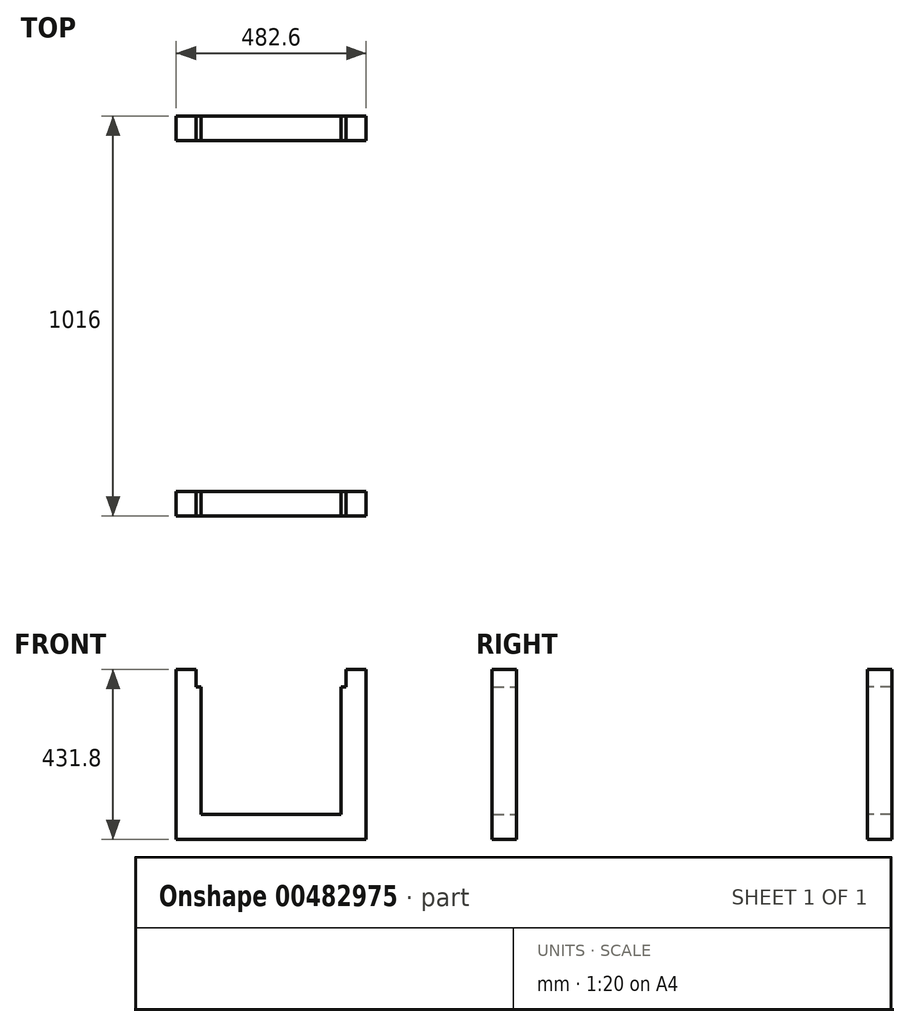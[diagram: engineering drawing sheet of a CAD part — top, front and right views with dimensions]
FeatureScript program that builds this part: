
annotation { "Feature Type Name" : "Feature", "Feature Type Description" : "" }
export const myFeature = defineFeature(function(context is Context, id is Id, definition is map)
    precondition{}
    {
        {
            var Q0;
            Q0=qCreatedBy(makeId("Front.planeOp"),FACE);
            var sketch = newSketch(context, id + "F0", { "sketchPlane" : qUnion([Q0])});
            skLineSegment(sketch, "E0.bottom", {"start": v(-93.2, 0) * mm, "end": v(-29.7, 0) * mm});
            skLineSegment(sketch, "E0.top", {"start": v(-93.2, -431.8) * mm, "end": v(-29.7, -431.8) * mm});
            skLineSegment(sketch, "E0.left", {"start": v(-93.2, 0) * mm, "end": v(-93.2, -431.8) * mm});
            skLineSegment(sketch, "E0.right", {"start": v(-29.7, 0) * mm, "end": v(-29.7, -431.8) * mm});
            skLineSegment(sketch, "E1.bottom", {"start": v(-93.2, 0) * mm, "end": v(389.4, 0) * mm});
            skLineSegment(sketch, "E1.top", {"start": v(-93.2, -431.8) * mm, "end": v(389.4, -431.8) * mm});
            skLineSegment(sketch, "E1.right", {"start": v(389.4, 0) * mm, "end": v(389.4, -431.8) * mm});
            skLineSegment(sketch, "E2.bottom", {"start": v(389.4, 0) * mm, "end": v(325.9, 0) * mm});
            skLineSegment(sketch, "E2.top", {"start": v(389.4, -431.8) * mm, "end": v(325.9, -431.8) * mm});
            skLineSegment(sketch, "E2.right", {"start": v(325.9, 0) * mm, "end": v(325.9, -431.8) * mm});
            skLineSegment(sketch, "E3.bottom", {"start": v(-29.7, -431.8) * mm, "end": v(325.9, -431.8) * mm});
            skLineSegment(sketch, "E3.top", {"start": v(-29.7, -368.3) * mm, "end": v(325.9, -368.3) * mm});
            skLineSegment(sketch, "E3.left", {"start": v(-29.7, -431.8) * mm, "end": v(-29.7, -368.3) * mm});
            skLineSegment(sketch, "E3.right", {"start": v(325.9, -431.8) * mm, "end": v(325.9, -368.3) * mm});
            skLineSegment(sketch, "E4.bottom", {"start": v(-29.7, 0) * mm, "end": v(-42.4, 0) * mm});
            skLineSegment(sketch, "E4.top", {"start": v(-29.7, -44.45) * mm, "end": v(-42.4, -44.45) * mm});
            skLineSegment(sketch, "E4.left", {"start": v(-29.7, 0) * mm, "end": v(-29.7, -44.45) * mm});
            skLineSegment(sketch, "E4.right", {"start": v(-42.4, 0) * mm, "end": v(-42.4, -44.45) * mm});
            skLineSegment(sketch, "E5", {"start": v(148.1, -431.8) * mm, "end": v(148.1, 0) * mm});
            skLineSegment(sketch, "E6.MirrorCS", {"start": v(325.9, -44.45) * mm, "end": v(338.6, -44.45) * mm});
            skLineSegment(sketch, "E7.MirrorCS", {"start": v(338.6, 0) * mm, "end": v(338.6, -44.45) * mm});
            skLineSegment(sketch, "E8.MirrorCS", {"start": v(325.9, 0) * mm, "end": v(338.6, 0) * mm});
            skLineSegment(sketch, "E9.MirrorCS", {"start": v(325.9, 0) * mm, "end": v(325.9, -44.45) * mm});
            skSolve(sketch);
        }
        {
            var Q0;
            {var subQ4=sQuery(id+"F0.wireOp",EDGE,"E0.top");Q0=makeQuery(id+"F0.imprint","IMPRINT",FACE,{"disambiguationData":[TD([[makeQuery(id+"F0.imprint","IMPRINT",EDGE,{"derivedFrom":subQ4}),1.0]])]});}
            var Q1;
            {var subQ1=sQuery(id+"F0.wireOp",EDGE,"E0.right");var subQ3=sQuery(id+"F0.wireOp",EDGE,"E3.top");var subQ4=makeQuery(id+"F0.imprint","INTERSECT",VERTEX,{"derivedFrom":[subQ1,subQ3]});Q1=makeQuery(id+"F0.imprint","IMPRINT",FACE,{"disambiguationData":[TD([[makeQuery(id+"F0.imprint","IMPRINT",EDGE,{"disambiguationData":[TD([[subQ4,-1.0]])],"derivedFrom":subQ3}),-1.0]])]});}
            var Q2;
            {var subQ0=sQuery(id+"F0.wireOp",EDGE,"E5");var subQ1=sQuery(id+"F0.wireOp",EDGE,"E1.top");var subQ2=makeQuery(id+"F0.imprint","INTERSECT",VERTEX,{"derivedFrom":[subQ1,subQ0]});Q2=makeQuery(id+"F0.imprint","IMPRINT",FACE,{"disambiguationData":[TD([[makeQuery(id+"F0.imprint","IMPRINT",EDGE,{"disambiguationData":[TD([[subQ2,-1.0]])],"derivedFrom":subQ1}),1.0]])]});}
            var Q3;
            {var subQ3=sQuery(id+"F0.wireOp",EDGE,"E1.right");Q3=makeQuery(id+"F0.imprint","IMPRINT",FACE,{"disambiguationData":[TD([[makeQuery(id+"F0.imprint","IMPRINT",EDGE,{"derivedFrom":subQ3}),-1.0]])]});}
            extrude(context, id + "F1", {"entities" : qUnion([Q0, Q1, Q2, Q3]), "depth" : 61.9 * mm, "offsetDistance" : 25.4 * mm});
        }
        {
            var Q0;
            Q0=sQuery(id+"F0.wireOp",EDGE,"E5");
            cPlane(context, id + "F2", {"entities" : qUnion([Q0]), "cplaneType" : CPlaneType.LINE_ANGLE, "offset" : 25.4 * mm, "angle" : 0 * degree, "width" : 152.4 * mm, "height" : 152.4 * mm});
        }
        {
            var Q0;
            Q0=qCreatedBy(id+"F2.planeOp",FACE);
            var sketch = newSketch(context, id + "F3", { "sketchPlane" : qUnion([Q0])});
            skLineSegment(sketch, "E10.bottom", {"start": v(-61.91, 0) * mm, "end": v(954.09, 0) * mm});
            skLineSegment(sketch, "E10.top", {"start": v(-61.91, -431.8) * mm, "end": v(954.09, -431.8) * mm});
            skLineSegment(sketch, "E10.left", {"start": v(-61.91, 0) * mm, "end": v(-61.91, -431.8) * mm});
            skLineSegment(sketch, "E10.right", {"start": v(954.09, 0) * mm, "end": v(954.09, -431.8) * mm});
            skLineSegment(sketch, "E11", {"start": v(446.09, 0) * mm, "end": v(446.09, -431.8) * mm});
            skSolve(sketch);
        }
        {
            var Q0;
            Q0=sQuery(id+"F3.wireOp",EDGE,"E11");
            cPlane(context, id + "F4", {"entities" : qUnion([Q0]), "cplaneType" : CPlaneType.LINE_ANGLE, "offset" : 25.4 * mm, "angle" : 90 * degree, "width" : 152.4 * mm, "height" : 152.4 * mm});
        }
        {
            var Q0;
            Q0=makeQuery(id+"F1.opExtrude","SWEPT_BODY",BODY,{"disambiguationData":[OSD([sQuery(id+"F0.wireOp",EDGE,"E0.bottom"),sQuery(id+"F0.wireOp",EDGE,"E0.top"),sQuery(id+"F0.wireOp",EDGE,"E0.left"),sQuery(id+"F0.wireOp",EDGE,"E0.right"),sQuery(id+"F0.wireOp",EDGE,"E1.bottom"),sQuery(id+"F0.wireOp",EDGE,"E1.top"),sQuery(id+"F0.wireOp",EDGE,"E1.right"),sQuery(id+"F0.wireOp",EDGE,"E2.right"),sQuery(id+"F0.wireOp",EDGE,"E3.top"),sQuery(id+"F0.wireOp",EDGE,"E4.top"),sQuery(id+"F0.wireOp",EDGE,"E4.right"),sQuery(id+"F0.wireOp",EDGE,"E6.MirrorCS"),sQuery(id+"F0.wireOp",EDGE,"E7.MirrorCS")])]});
            var Q1;
            Q1=qCreatedBy(id+"F4.planeOp",FACE);
            mirror(context, id + "F5", {"entities" : qUnion([Q0]), "mirrorPlane" : qUnion([Q1])});
        }
    });
